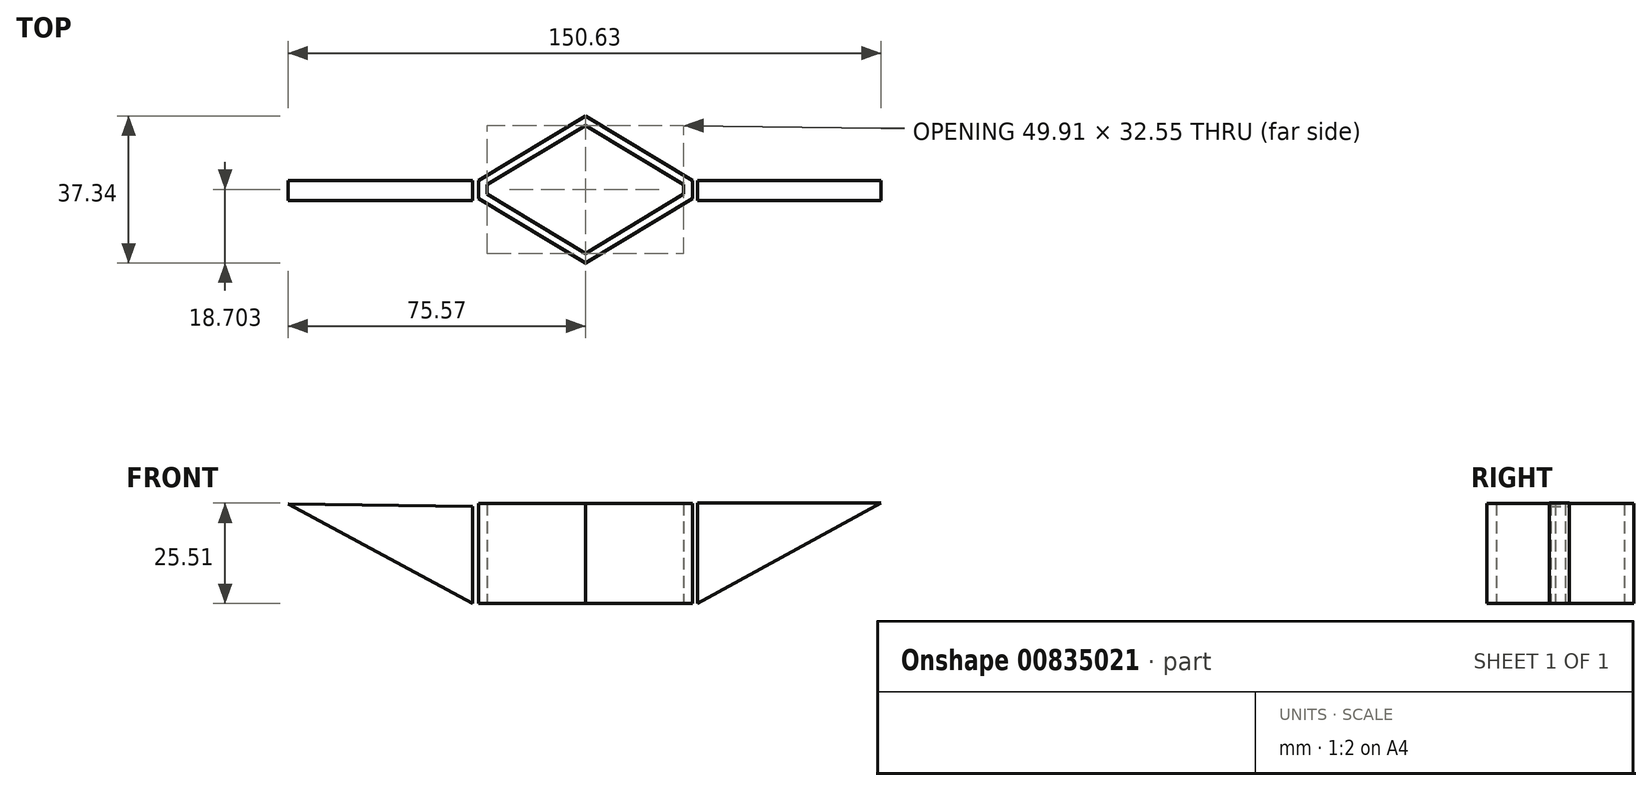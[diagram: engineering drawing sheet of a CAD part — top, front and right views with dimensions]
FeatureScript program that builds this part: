
annotation { "Feature Type Name" : "Feature", "Feature Type Description" : "" }
export const myFeature = defineFeature(function(context is Context, id is Id, definition is map)
    precondition{}
    {
        {
            var Q0;
            Q0=qCreatedBy(makeId("Front.planeOp"),FACE);
            var sketch = newSketch(context, id + "F0", { "sketchPlane" : qUnion([Q0])});
            skLineSegment(sketch, "E0", {"start": v(-75.56, 25.35) * mm, "end": v(-28.75, 0) * mm});
            skLineSegment(sketch, "E1", {"start": v(28.42, 0) * mm, "end": v(28.42, 25.5) * mm});
            skLineSegment(sketch, "E2", {"start": v(-75.56, 25.35) * mm, "end": v(-28.75, 24.7) * mm});
            skLineSegment(sketch, "E3", {"start": v(-28.75, 24.7) * mm, "end": v(-28.75, 0) * mm});
            skLineSegment(sketch, "E4", {"start": v(28.42, 25.5) * mm, "end": v(75.07, 25.5) * mm});
            skLineSegment(sketch, "E5", {"start": v(75.07, 25.5) * mm, "end": v(28.42, 0) * mm});
            skSolve(sketch);
        }
        {
            var Q0;
            Q0 = qSketchRegion(id + "F0", true);
            extrude(context, id + "F1", {"entities" : qUnion([Q0]), "depth" : 5.08 * mm, "offsetDistance" : 25.4 * mm});
        }
        {
            var Q0;
            Q0=qCreatedBy(makeId("Top.planeOp"),FACE);
            var sketch = newSketch(context, id + "F2", { "sketchPlane" : qUnion([Q0])});
            skLineSegment(sketch, "E6", {"start": v(-27.13, 0) * mm, "end": v(-27.13, -4.62) * mm});
            skLineSegment(sketch, "E7", {"start": v(-27.13, -4.62) * mm, "end": v(0, -20.97) * mm});
            skLineSegment(sketch, "E8", {"start": v(0, -20.97) * mm, "end": v(27.15, -4.62) * mm});
            skLineSegment(sketch, "E9", {"start": v(27.15, -4.62) * mm, "end": v(27.15, 0) * mm});
            skLineSegment(sketch, "E10", {"start": v(27.15, 0) * mm, "end": v(0, 16.37) * mm});
            skLineSegment(sketch, "E11", {"start": v(0, 16.37) * mm, "end": v(-27.13, 0) * mm});
            skLineSegment(sketch, "E12", {"start": v(0, 14) * mm, "end": v(-24.94, -1.04) * mm});
            skLineSegment(sketch, "E13", {"start": v(0, -18.54) * mm, "end": v(-24.94, -3.5) * mm});
            skLineSegment(sketch, "E14", {"start": v(-24.94, -3.5) * mm, "end": v(-24.94, -1.04) * mm});
            skLineSegment(sketch, "E15", {"start": v(0, 14) * mm, "end": v(24.96, -1.04) * mm});
            skLineSegment(sketch, "E16", {"start": v(24.96, -1.04) * mm, "end": v(24.96, -3.48) * mm});
            skLineSegment(sketch, "E17", {"start": v(24.96, -3.48) * mm, "end": v(0, -18.54) * mm});
            skSolve(sketch);
        }
        {
            var Q0;
            Q0 = qSketchRegion(id + "F2", true);
            extrude(context, id + "F3", {"entities" : qUnion([Q0]), "depth" : 25.4 * mm, "offsetDistance" : 25.4 * mm});
        }
    });
